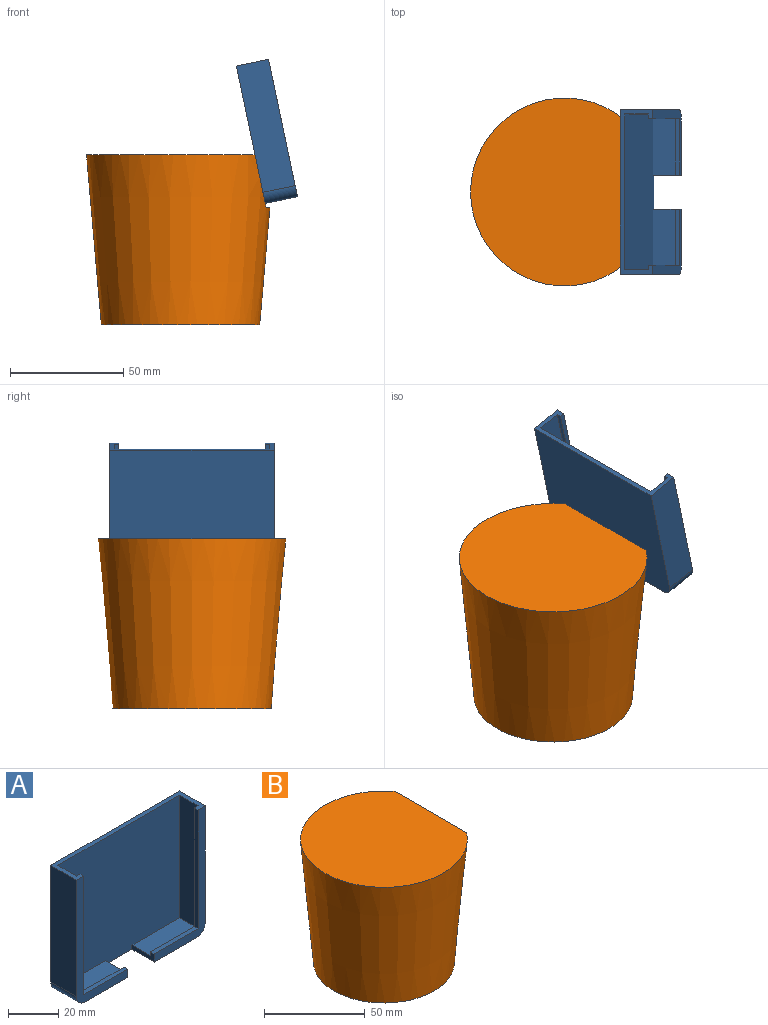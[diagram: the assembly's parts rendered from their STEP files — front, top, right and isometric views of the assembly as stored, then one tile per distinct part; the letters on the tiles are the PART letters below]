
ASSEMBLY  parts=2 mates=1
PART A: 22 faces, bbox 72.8x14.5x62 mm
  f0: plane 24.9x2mm, normal (0,0,1), area 49.8mm2, adj f1,f13,f17,f21
  f1: plane 62x28.9mm, normal (0,-1,0), area 342.2mm2, adj f0,f5,f6,f7,f17,f19,f21
  f2: plane 26.9x10.5mm, normal (0,0,1), area 282.5mm2, adj f3,f8,f10,f20
  f3: plane 60x26.9mm, normal (0,1,0), area 169.8mm2, adj f2,f7,f10,f14,f16,f20
  f4: plane 57x14.5mm, normal (-1,0,0), area 826.5mm2, adj f7,f9,f15,f18
  f5: plane 62.8x14.5mm, normal (0,0,-1), area 723.1mm2, adj f1,f8,f9,f15,f18,f19,f20,f21
  f6: plane 57x14.5mm, normal (1,0,0), area 826.5mm2, adj f1,f7,f9,f19
  f7: plane 72.8x14.5mm, normal (0,0,1), area 203.6mm2, adj f1,f3,f4,f6,f8,f9,f10,f11
  f8: plane 68.8x62mm, normal (0,-1,0), area 4158mm2, adj f2,f5,f7,f10,f11,f12,f20,f21
  f9: plane 72.8x62mm, normal (0,1,0), area 4502.9mm2, adj f4,f5,f6,f7,f18,f19
  f10: plane 60x10.5mm, normal (1,0,0), area 630mm2, adj f2,f3,f7,f8
  f11: plane 60x10.5mm, normal (-1,0,0), area 630mm2, adj f7,f8,f12,f13
  f12: plane 26.9x10.5mm, normal (0,0,1), area 282.4mm2, adj f8,f11,f13,f21
  f13: plane 60x26.9mm, normal (0,1,0), area 169.8mm2, adj f0,f7,f11,f12,f17,f21
  f14: plane 24.9x2mm, normal (0,0,1), area 49.8mm2, adj f3,f15,f16,f20
  f15: plane 62x28.9mm, normal (0,-1,0), area 342.2mm2, adj f4,f5,f7,f14,f16,f18,f20
  f16: plane 58x2mm, normal (1,0,0), area 116mm2, adj f3,f7,f14,f15
  f17: plane 58x2mm, normal (-1,0,0), area 116mm2, adj f0,f1,f7,f13
  f18: cylinder r=5mm len=14.5mm, axis (0,1,0), area 113.9mm2, adj f4,f5,f9,f15
  f19: cylinder r=5mm len=14.5mm, axis (0,-1,0), area 113.9mm2, adj f1,f5,f6,f9
  f20: plane 12.5x4mm, normal (1,0,0), area 29mm2, adj f2,f3,f5,f8,f14,f15
  f21: plane 12.5x4mm, normal (-1,0,0), area 29mm2, adj f0,f1,f5,f8,f12,f13
PART B: 7 faces, bbox 83x83x75 mm
  f0: plane 83x74.48mm, normal (0,0,1), area 5118mm2, adj f2,f3
  f1: plane 70x70mm, normal (0,0,-1), area 322.8mm2, adj f2,f5
  f2: cone r=41.5mm half-angle=5deg, axis (0,0,1), area 17158.1mm2, adj f0,f1,f3,f4
  f3: plane 50.38x23.1mm, normal (0.98,0,0.21), area 907.8mm2, adj f0,f2,f4
  f4: plane 22.7x1.67mm, normal (0,0,1), area 25.3mm2, adj f2,f3
  f5: cylinder r=33.5mm len=67mm, axis (0,0,-1), area 11155.8mm2, adj f1,f6
  f6: plane 67x67mm, normal (0,0,-1), area 3525.7mm2, adj f5
PLACE A rot(axis=(-0.1,-0.1,0.99),90.6deg) t=(22.14,10.34,70.58)mm
PLACE B t=(-8.96,10.34,-13.37)mm fixed
MATE fastened A.f9 <-> B.f3  axis (-0.98,0,-0.21) through (26.16,10.34,51.43)mm
